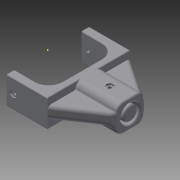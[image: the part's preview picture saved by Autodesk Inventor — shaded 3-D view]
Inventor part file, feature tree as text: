
AUTODESK INVENTOR PART (.ipt)
format: ipt  version: 2014 (Build 180170000, 170)  size: 860,160 bytes
history: native  units: mm
features: sketch x22, extrude x15, fillet x12, plane x4, emboss x1
ambient origin geometry x8: Origin, YZ Plane, XZ Plane, XY Plane, X Axis, Y Axis, Z Axis, Center Point
bodies: Solid1 (feature_tree)
feature tree (54):
  extrude  "Extrusion1"  Depth=76.2mm
  extrude  "Extrusion2"  Depth=63.5mm
  extrude  "Extrusion4"  Depth=50.8mm TaperAngle=0.0deg
  sketch  "Sketch5"  dims[d11=12.7mm d12=6.604mm]
  sketch  "Sketch6"  dims[d13=50.8mm d14=0.0mm d20=34.0868mm d21=26.3398mm d22=76.2mm d23=0.0mm d24=25.4mm d25=0.0mm d26=25.4mm d27=0.0mm d28=12.7mm d33=6.35mm d34=3.175mm d35=3.175mm d36=3.175mm]
  plane  "Work Plane1"
  extrude  "Extrusion5"  Depth=6.604mm
  sketch  "Sketch8"  dims[d41=0.25mm d42=6.21mm]
  sketch  "Sketch9"  dims[d43=11.5mm d44=11.3665mm]
  plane  "Work Plane2"
  extrude  "Extrusion6"  Depth=3.175mm
  fillet  "Fillet1"  Radius=26.3398mm
  fillet  "Fillet6"  Radius=76.2mm
  fillet  "Fillet7"  Radius=25.4mm
  fillet  "Fillet8"  Radius=25.4mm
  fillet  "Fillet9"  Radius=12.7mm
  fillet  "Fillet12"  Radius=6.35mm
  fillet  "Fillet13"  Radius=3.175mm
  fillet  "Fillet14"  Radius=3.175mm
  fillet  "Fillet15"  Radius=3.175mm
  extrude  "Extrusion7"  Depth=3.175mm
  plane  "Work Plane4"
  extrude  "Extrusion8"  Depth=6.21mm
  sketch  "Sketch13"  dims[d54=3.0mm d55=0.0mm d56=16.383mm]
  sketch  "Sketch15"  dims[d57=7.0mm d58=0.0mm d59=16.383mm]
  extrude  "Extrusion9"  Depth=11.3665mm
  plane  "Work Plane5"
  extrude  "Extrusion10"  Depth=25.4mm
  extrude  "Extrusion11"  Depth=114.3mm
  extrude  "Extrusion12"  Depth=11.3665mm
  extrude  "Extrusion13"  Depth=16.383mm
  extrude  "Extrusion14"  Depth=16.383mm
  extrude  "Extrusion15"  Depth=6.35mm
  extrude  "Extrusion16"  Depth=6.35mm
  fillet  "Fillet20"  Radius=6.35mm
  fillet  "Fillet21"  Radius=147.4mm
  fillet  "Fillet22"  Radius=5.0mm
  emboss  "Emboss1"
  sketch  "Sketch1"  dims[d0=76.2mm d1=76.2mm]
  sketch  "Sketch2"  dims[d2=15.0mm d3=63.5mm]
  sketch  "Sketch4"  dims[d8=76.2mm d9=50.8mm d10=0.0mm]
  sketch  "Sketch7"  dims[d39=3.175mm d40=50.8mm]
  sketch  "Sketch10"  dims[d45=3.0mm d46=0.0mm d48=25.4mm]
  sketch  "Sketch11"  dims[d49=6.604mm d50=114.3mm]
  sketch  "Sketch12"  dims[d51=4.0mm d52=0.0mm d53=11.3665mm]
  sketch  "Sketch16"  dims[d60=6.0mm d61=0.0mm d66=6.35mm]
  sketch  "Sketch17"  dims[d67=6.35mm d68=6.35mm d69=6.35mm d70=147.4mm d71=0.0mm d72=5.0mm d73=0.0mm]
  sketch  "Sketch18"  dims[d74=6.35mm]
  sketch  "Sketch19"  dims[d75=6.35mm]
  sketch  "Sketch20"  dims[d76=6.35mm]
  sketch  "Sketch21"  dims[d77=76.2mm]
  sketch  "Sketch22"  dims[d78=71.2mm d79=0.0mm]
  sketch  "Sketch25"  dims[d80=76.2mm]
  sketch  "Sketch26"  dims[d81=5.0mm d82=0.0mm d87=25.0mm d88=25.0mm d89=50.8mm d90=0.0mm d91=2.0mm d92=2.0mm d93=2.0mm d94=19.05mm d95=2.0mm d96=0.0mm]
